# Revit family: DistanzrohrAbschnitt
name_source: partatom
category: HLS-Bauteile
revit_build: Autodesk Revit 2018 (Build: 20190510_1515(x64)
units: mm (PartAtom-declared; Revit-internal decimal feet)

## family parameters
Arbeitsebenenbasiert = Ja
Beim Laden mit Abzugskörper schneiden = Nein
Bemaßung runder Anschluss = Durchmesser verwenden
Gemeinsam genutzt = Ja
Immer vertikal = Nein
Raumberechnungspunkt = Nein
Teiletyp = Normal

## types (2) — shared parameters
D = 21 mm  [stored 0.0688976 ft]
Fabrikat = MEFA
Kurztext1 = Distanzrohr 1/2"
Länge = 100 mm  [stored 0.328084 ft]
Material = Stahl
Thread = 1/2''
Vorgabe-Ansicht = 1219 mm
zero-valued in all types: Breite, Fläche (schwächster Profilquerschnitt), Stärke

## per-type parameters (varying)
| type | Artikelnummer | Gewicht | Kurztext2 | vpe |
| Distanzrohr 1/2" Abschnitt L=100mm | 07070100 | 0.11 kg | Länge 100 mm gvz | 10 |
| Distanzrohr 1/2" Abschnitt L=150mm | 07070150 | 0.17 kg | Länge 150 mm gvz | 25 |

note: [stored X ft] marks values corroborated as IEEE doubles in the binary element streams (Revit-internal decimal feet)
